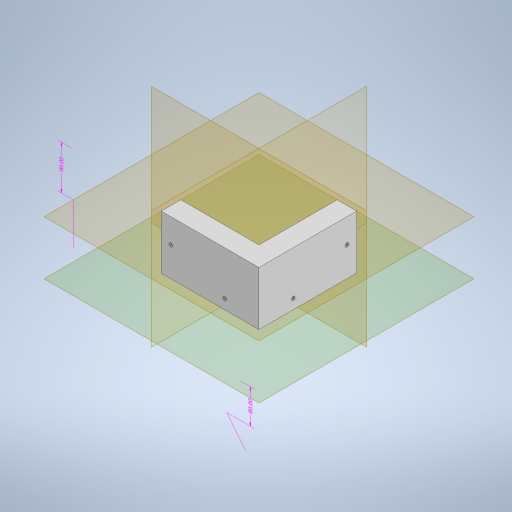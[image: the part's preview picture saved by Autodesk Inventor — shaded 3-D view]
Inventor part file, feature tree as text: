
AUTODESK INVENTOR PART (.ipt)
format: ipt  version: 2023 (Build 270158000, 158)  size: 429,056 bytes
history: native  units: mm
features: sketch x9, extrude x5, other x4, hole x4, plane x4, split x4
ambient origin geometry x8: Origin, YZ Plane, XZ Plane, XY Plane, X Axis, Y Axis, Z Axis, Center Point
bodies: Body1 (feature_tree)
feature tree (30):
  other  "Sólido1"
  other  "Anotaciones"
  extrude  "Extrusión1"  Depth=200.0mm
  hole  "Agujero1"  [1 undecoded]
  extrude  "Extrusión2"  Depth=15.0mm
  extrude  "Extrusión3"  Depth=80.0mm TaperAngle=0.0deg
  extrude  "Extrusión4"  Depth=200.0mm
  extrude  "Extrusión5"  Depth=20.0mm
  hole  "Agujero2"  [1 undecoded]
  plane  "Plano de trabajo1"
  split  "Dividir1"
  plane  "Plano de trabajo2"
  plane  "Plano de trabajo3"
  sketch  "Boceto9"  dims[d37=20.0mm d38=20.0mm]
  plane  "Plano de trabajo4"
  hole  "Agujero3"  [1 undecoded]
  hole  "Agujero4"  [1 undecoded]
  split  "Dividir2"
  split  "Dividir3"
  split  "Dividir4"
  sketch  "Boceto2"  dims[d7=15.0mm d8=200.0mm]
  sketch  "Boceto3"  dims[d9=10.0mm d10=0.0mm]
  sketch  "Boceto4"  dims[d12=1.75mm d13=1.75mm d14=1.75mm d15=1.75mm d16=10.0mm d17=10.0mm d19=30.0mm]
  sketch  "Boceto5"  dims[d20=3.5mm d21=6.0mm d22=4.0mm d23=2.0mm d24=90.0deg d25=8.0mm d26=20.594885mm d27=15.0mm]
  sketch  "Boceto6"  dims[d28=20.0mm d29=80.0mm d30=0.0mm]
  sketch  "Boceto7"  dims[d31=48.0mm d32=200.0mm]
  sketch  "Boceto8"  dims[d33=110.0mm d34=0.0mm d36=20.0mm]
  sketch  "Boceto10"  dims[d39=90.0mm d40=0.0mm d42=10.0mm d43=30.0mm d44=0.0mm d46=1.75mm d47=1.75mm d48=1.75mm d49=1.75mm d50=10.0mm d51=10.0mm d52=15.0mm d56=3.5mm d57=6.0mm d58=4.0mm d59=2.0mm d60=90.0deg d61=8.0mm d62=20.594885mm d63=10.0mm d65=10.0mm d66=10.0mm d67=31.75mm d70=15.0mm d74=200.0mm d78=20.0mm d82=90.0deg d83=10.0mm d84=30.0mm d85=5.0mm d86=5.0mm d87=5.0mm d88=5.0mm d89=20.0mm d91=30.0mm d92=5.0mm d93=5.0mm d94=3.5mm d95=5.0mm d96=5.0mm d97=5.0mm d98=5.0mm d99=5.0mm d100=20.0mm d101=3.5mm d102=6.0mm d103=4.0mm d104=2.0mm d105=90.0deg d106=8.0mm d107=20.594885mm d108=10.0mm d109=30.0mm d110=5.0mm d111=5.0mm d112=5.0mm d113=5.0mm d114=5.0mm d115=5.0mm d116=3.5mm d117=5.0mm d118=5.0mm d119=5.0mm d120=5.0mm d121=5.0mm d122=30.0mm d123=30.0mm d124=3.5mm d125=6.0mm d126=4.0mm d127=2.0mm d128=90.0deg d129=8.0mm d130=20.594885mm d75=1.454734mm d76=6.982969mm d77=80.0mm d79=4.097996mm d80=1.406125mm d81=90.0mm]
  other  "Cota lineal 2"
  other  "Cota lineal 3"
note: 4 required parameter values undecoded (feature->parameter linkage not recoverable at this tier; creation-order binding heuristic only, values carry confidence <= 0.55)
